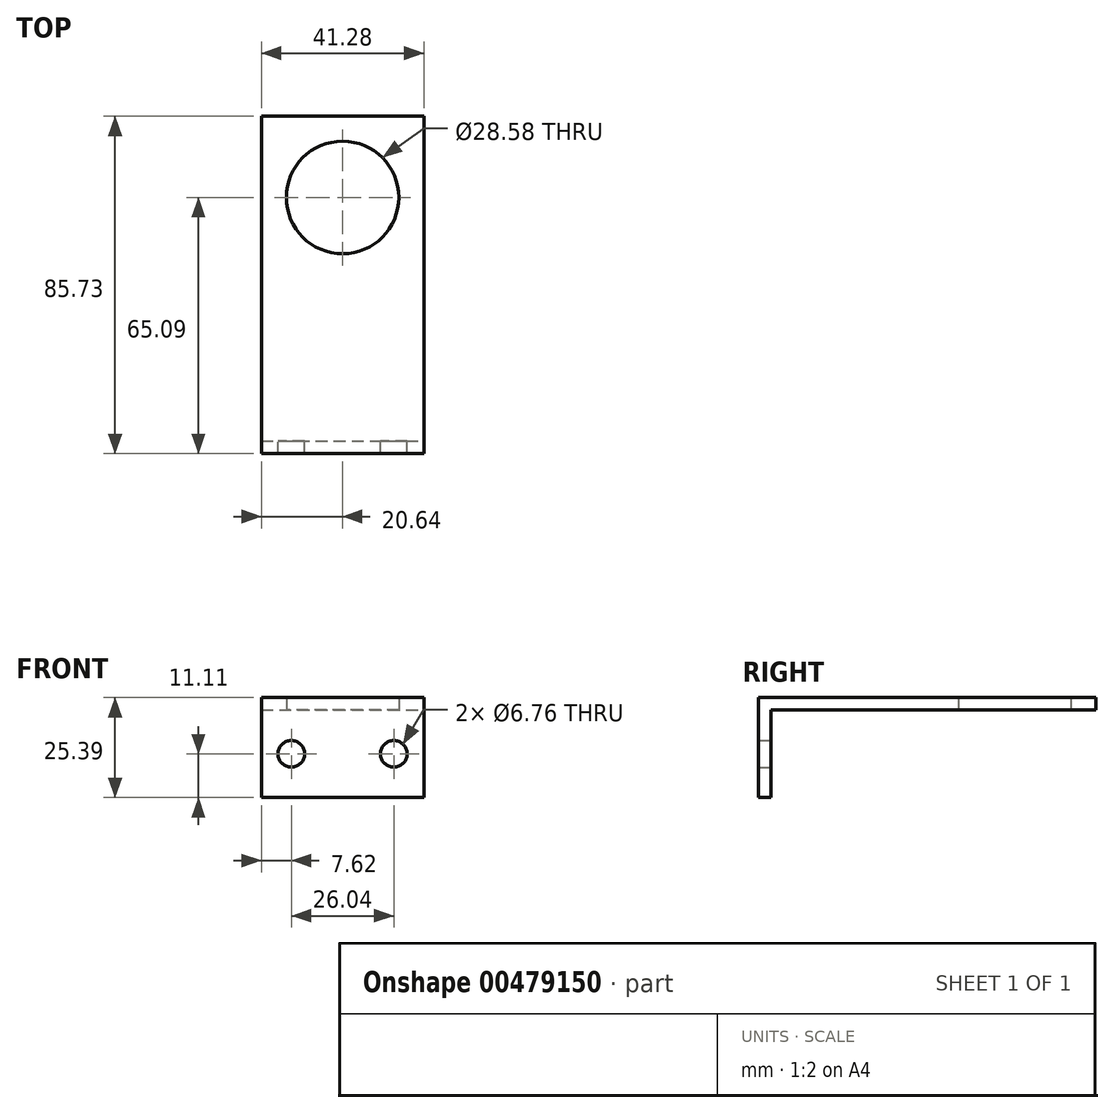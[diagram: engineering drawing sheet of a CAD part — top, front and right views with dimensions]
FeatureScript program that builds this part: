
annotation { "Feature Type Name" : "Feature", "Feature Type Description" : "" }
export const myFeature = defineFeature(function(context is Context, id is Id, definition is map)
    precondition{}
    {
        {
            var Q0;
            Q0=qCreatedBy(makeId("Top.planeOp"),FACE);
            var sketch = newSketch(context, id + "F0", { "sketchPlane" : qUnion([Q0])});
            skLineSegment(sketch, "E0.bottom", {"start": v(-42.49, 30.34) * mm, "end": v(-1.21, 30.34) * mm});
            skLineSegment(sketch, "E0.top", {"start": v(-42.49, -55.39) * mm, "end": v(-1.21, -55.39) * mm});
            skLineSegment(sketch, "E0.left", {"start": v(-42.49, 30.34) * mm, "end": v(-42.49, -55.39) * mm});
            skLineSegment(sketch, "E0.right", {"start": v(-1.21, 30.34) * mm, "end": v(-1.21, -55.39) * mm});
            skCircle(sketch, "E1", {"center": v(-21.85, 9.7) * mm, "radius": 14.29 * mm});
            skLineSegment(sketch, "E2.top", {"start": v(-42.49, -52.21) * mm, "end": v(-1.21, -52.21) * mm});
            skLineSegment(sketch, "E2.left", {"start": v(-42.49, -55.39) * mm, "end": v(-42.49, -52.21) * mm});
            skLineSegment(sketch, "E2.right", {"start": v(-1.21, -55.39) * mm, "end": v(-1.21, -52.21) * mm});
            skSolve(sketch);
        }
        {
            var Q0;
            Q0 = qSketchRegion(id + "F0", true);
            extrude(context, id + "F1", {"entities" : qUnion([Q0]), "depth" : 3.17 * mm});
        }
        {
            var Q0;
            Q0=makeQuery(id+"F0.imprint","IMPRINT",FACE,{"disambiguationData":[TD([[makeQuery(id+"F0.imprint","IMPRINT",EDGE,{"derivedFrom":sQuery(id+"F0.wireOp",EDGE,"E0.top")}),1.0]])]});
            extrude(context, id + "F2", {"entities" : qUnion([Q0]), "operationType" : NewBodyOperationType.ADD, "oppositeDirection" : true, "depth" : 22.22 * mm});
        }
        {
            var Q0;
            Q0=makeQuery(id+"F2.opExtrude","SWEPT_FACE",FACE,{"disambiguationData":[OSD([sQuery(id+"F0.wireOp",EDGE,"E2.top")])]});
            var sketch = newSketch(context, id + "F3", { "sketchPlane" : qUnion([Q0])});
            skPoint(sketch, "E3", {"position": v(8.83, -11.11) * mm});
            skPoint(sketch, "E4", {"position": v(34.87, -11.11) * mm});
            skSolve(sketch);
        }
        {
            var Q0;
            Q0=sQuery(id+"F3.wireOp",VERTEX,"E3");
            var Q1;
            Q1=sQuery(id+"F3.wireOp",VERTEX,"E4");
            var Q2;
            Q2=makeQuery(id+"F1.opExtrude","SWEPT_BODY",BODY,{"disambiguationData":[OSD([sQuery(id+"F0.wireOp",EDGE,"E0.bottom"),sQuery(id+"F0.wireOp",EDGE,"E0.left"),sQuery(id+"F0.wireOp",EDGE,"E0.right"),sQuery(id+"F0.wireOp",EDGE,"E1"),sQuery(id+"F0.wireOp",EDGE,"E0.top"),sQuery(id+"F0.wireOp",EDGE,"E2.left"),sQuery(id+"F0.wireOp",EDGE,"E2.right")])]});
            hole(context, id + "F4", {"style" : HoleStyle.SIMPLE, "endStyle" : HoleEndStyle.BLIND, "standardTappedOrClearance" : lookupTablePath({ "standard" : "ANSI", "fit" : "Normal (ASME)", "size" : "1/4", "type" : "Clearance" }), "standardBlindInLast" : lookupTablePath({ "fit" : "Free", "standard" : "ANSI", "size" : "1/4", "type" : "Clearance" }), "holeDiameter" : 6.76 * mm, "holeDepth" : 76.2 * mm, "isTappedThrough" : true, "tappedDepth" : 12.7 * mm, "tapClearance" : 3, "startFromSketch" : true, "locations" : qUnion([Q0, Q1]), "scope" : qUnion([Q2])});
        }
    });
